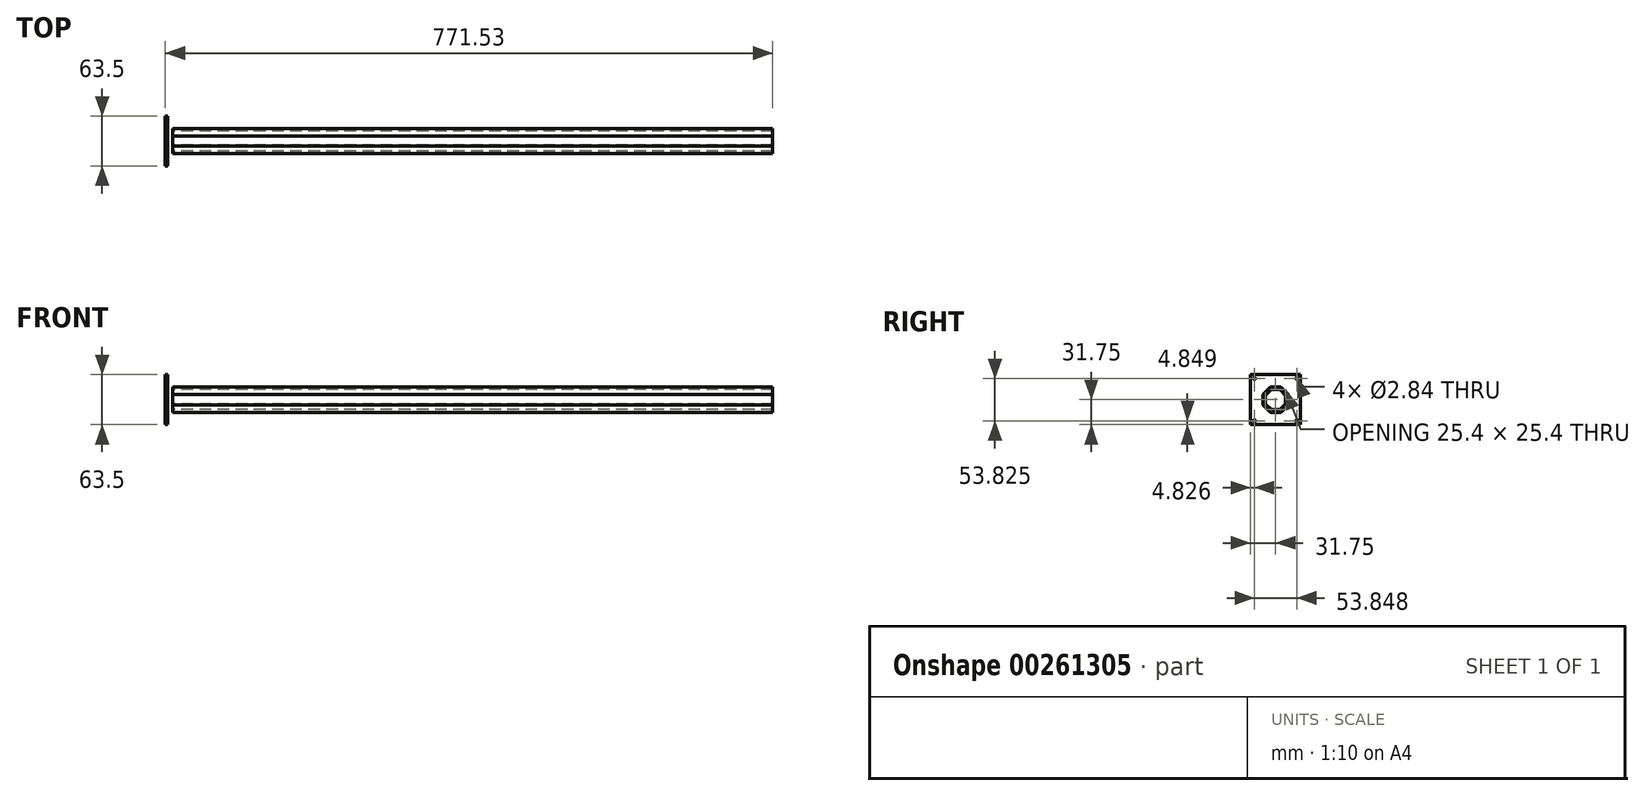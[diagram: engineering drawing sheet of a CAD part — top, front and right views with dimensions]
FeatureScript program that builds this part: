
annotation { "Feature Type Name" : "Feature", "Feature Type Description" : "" }
export const myFeature = defineFeature(function(context is Context, id is Id, definition is map)
    precondition{}
    {
        {
            var Q0;
            Q0=qCreatedBy(makeId("Right.planeOp"),FACE);
            var sketch = newSketch(context, id + "F0", { "sketchPlane" : qUnion([Q0])});
            skCircle(sketch, "E0.cCircle", {"center": v(0, 0) * mm, "radius": 12.7 * mm, "construction": true});
            skLineSegment(sketch, "E0.0", {"start": v(-5.26, 12.7) * mm, "end": v(5.26, 12.7) * mm});
            skLineSegment(sketch, "E0.1", {"start": v(5.26, 12.7) * mm, "end": v(12.7, 5.26) * mm});
            skLineSegment(sketch, "E0.2", {"start": v(12.7, 5.26) * mm, "end": v(12.7, -5.26) * mm});
            skLineSegment(sketch, "E0.3", {"start": v(12.7, -5.26) * mm, "end": v(5.26, -12.7) * mm});
            skLineSegment(sketch, "E0.4", {"start": v(5.26, -12.7) * mm, "end": v(-5.26, -12.7) * mm});
            skLineSegment(sketch, "E0.5", {"start": v(-5.26, -12.7) * mm, "end": v(-12.7, -5.26) * mm});
            skLineSegment(sketch, "E0.6", {"start": v(-12.7, -5.26) * mm, "end": v(-12.7, 5.26) * mm});
            skLineSegment(sketch, "E0.7", {"start": v(-12.7, 5.26) * mm, "end": v(-5.26, 12.7) * mm});
            skPoint(sketch, "E0.0.midPoint", {"position": v(0, 12.7) * mm});
            skCircle(sketch, "E1.cCircle", {"center": v(0, 0) * mm, "radius": 16 * mm, "construction": true});
            skLineSegment(sketch, "E1.0", {"start": v(-6.63, 16) * mm, "end": v(6.63, 16) * mm});
            skLineSegment(sketch, "E1.1", {"start": v(6.63, 16) * mm, "end": v(16, 6.63) * mm});
            skLineSegment(sketch, "E1.2", {"start": v(16, 6.63) * mm, "end": v(16, -6.63) * mm});
            skLineSegment(sketch, "E1.3", {"start": v(16, -6.63) * mm, "end": v(6.63, -16) * mm});
            skLineSegment(sketch, "E1.4", {"start": v(6.63, -16) * mm, "end": v(-6.63, -16) * mm});
            skLineSegment(sketch, "E1.5", {"start": v(-6.63, -16) * mm, "end": v(-16, -6.63) * mm});
            skLineSegment(sketch, "E1.6", {"start": v(-16, -6.63) * mm, "end": v(-16, 6.63) * mm});
            skLineSegment(sketch, "E1.7", {"start": v(-16, 6.63) * mm, "end": v(-6.63, 16) * mm});
            skPoint(sketch, "E1.0.midPoint", {"position": v(0, 16) * mm});
            skSolve(sketch);
        }
        {
            var Q0;
            Q0=makeQuery(id+"F0.imprint","IMPRINT",FACE,{"disambiguationData":[TD([[makeQuery(id+"F0.imprint","IMPRINT",EDGE,{"derivedFrom":sQuery(id+"F0.wireOp",EDGE,"E0.0")}),1.0]])]});
            extrude(context, id + "F1", {"entities" : qUnion([Q0]), "depth" : 762 * mm});
        }
        {
            var Q0;
            Q0=qCreatedBy(makeId("Right.planeOp"),FACE);
            cPlane(context, id + "F2", {"entities" : qUnion([Q0]), "cplaneType" : CPlaneType.OFFSET, "offset" : 6.35 * mm, "oppositeDirection" : true, "width" : 150 * mm, "height" : 150 * mm});
        }
        {
            var Q0;
            Q0=qCreatedBy(id+"F2.planeOp",FACE);
            var sketch = newSketch(context, id + "F3", { "sketchPlane" : qUnion([Q0])});
            skCircle(sketch, "E2", {"center": v(0, 0) * mm, "radius": 19.09 * mm});
            skLineSegment(sketch, "E3", {"start": v(0, 0) * mm, "end": v(0, 22.66) * mm, "construction": true});
            skPoint(sketch, "E4", {"position": v(0, 19.09) * mm});
            skSolve(sketch);
        }
        {
            var Q0;
            Q0=qCreatedBy(makeId("Right.planeOp"),FACE);
            var sketch = newSketch(context, id + "F4", { "sketchPlane" : qUnion([Q0])});
            skCircle(sketch, "E5", {"center": v(0, 0) * mm, "radius": 16 * mm});
            skSolve(sketch);
        }
        {
            var Q0;
            Q0=qCreatedBy(makeId("Front.planeOp"),FACE);
            var sketch = newSketch(context, id + "F5", { "sketchPlane" : qUnion([Q0])});
            skLineSegment(sketch, "E6", {"start": v(0, -16) * mm, "end": v(0, 16) * mm});
            skLineSegment(sketch, "E7.1.0", {"start": v(0, 6.63) * mm, "end": v(0, 16) * mm});
            skLineSegment(sketch, "E7.1.2", {"start": v(0, 16) * mm, "end": v(0, 6.63) * mm});
            skLineSegment(sketch, "E7.1.3", {"start": v(0, 6.63) * mm, "end": v(0, -6.63) * mm});
            skLineSegment(sketch, "E7.1.4", {"start": v(0, -6.63) * mm, "end": v(0, -16) * mm});
            skLineSegment(sketch, "E7.1.6", {"start": v(0, -16) * mm, "end": v(0, -6.63) * mm});
            skLineSegment(sketch, "E7.1.7", {"start": v(0, -6.63) * mm, "end": v(0, 6.63) * mm});
            skLineSegment(sketch, "E8.0", {"start": v(-6.35, 19.09) * mm, "end": v(-6.35, -19.09) * mm});
            skArc(sketch, "E9", {"start": v(-6.35, 19.09) * mm, "mid": v(-3.6, 16.68) * mm, "end": v(0, 16) * mm});
            skSolve(sketch);
        }
        {
            var Q0;
            Q0=sQuery(id+"F4.wireOp",EDGE,"E5");
            var Q1;
            Q1=sQuery(id+"F3.wireOp",EDGE,"E2");
            var Q2;
            Q2=sQuery(id+"F5.wireOp",EDGE,"E9");
            loft(context, id + "F6", {"bodyType" : ToolBodyType.SURFACE, "addGuides" : true, "wireProfilesArray" : [{ "wireProfileEntities" : qUnion([Q0]) }, { "wireProfileEntities" : qUnion([Q1]) }], "guidesArray" : [{ "guideEntities" : qUnion([Q2]), "guideDerivativeType" : LoftGuideDerivativeType.DEFAULT, "guideDerivativeMagnitude" : 1 }]});
        }
        {
            var Q0;
            Q0=qCreatedBy(id+"F2.planeOp",FACE);
            var sketch = newSketch(context, id + "F7", { "sketchPlane" : qUnion([Q0])});
            skPoint(sketch, "E10.middle", {"position": v(0, 0) * mm});
            skArc(sketch, "E11.0", {"start": v(-14.94, -11.87) * mm, "mid": v(-19.09, 0) * mm, "end": v(-14.94, 11.87) * mm});
            skLineSegment(sketch, "E12.trimOffspring", {"start": v(31.75, 31.75) * mm, "end": v(31.75, 32.75) * mm});
            skLineSegment(sketch, "E13.trimOffspring", {"start": v(-31.75, 31.75) * mm, "end": v(-31.75, 32.75) * mm});
            skArc(sketch, "E14.trimOffspring", {"start": v(14.94, 11.87) * mm, "mid": v(19.09, 0) * mm, "end": v(14.94, -11.87) * mm});
            skLineSegment(sketch, "E15.bottom", {"start": v(-31.75, 31.75) * mm, "end": v(31.75, 31.75) * mm});
            skLineSegment(sketch, "E15.top", {"start": v(-31.75, -31.75) * mm, "end": v(31.75, -31.75) * mm});
            skLineSegment(sketch, "E15.left", {"start": v(-31.75, 31.75) * mm, "end": v(-31.75, -31.75) * mm});
            skLineSegment(sketch, "E15.right", {"start": v(31.75, 31.75) * mm, "end": v(31.75, -31.75) * mm});
            skSolve(sketch);
        }
        {
            var Q0;
            Q0 = qSketchRegion(id + "F7", true);
            extrude(context, id + "F8", {"entities" : qUnion([Q0]), "oppositeDirection" : true, "depth" : 3.17 * mm});
        }
        {
            var Q0;
            Q0=makeQuery(id+"F8.opExtrude","CAP_FACE",FACE,{"disambiguationData":[OSD([sQuery(id+"F7.wireOp",EDGE,"E15.bottom"),sQuery(id+"F7.wireOp",EDGE,"E15.top"),sQuery(id+"F7.wireOp",EDGE,"E15.left"),sQuery(id+"F7.wireOp",EDGE,"E15.right")])],"isStart":true});
            var sketch = newSketch(context, id + "F9", { "sketchPlane" : qUnion([Q0])});
            skPoint(sketch, "E16", {"position": v(-26.92, 26.92) * mm});
            skPoint(sketch, "E17", {"position": v(26.92, 26.92) * mm});
            skPoint(sketch, "E18", {"position": v(26.92, -26.9) * mm});
            skPoint(sketch, "E19", {"position": v(-26.92, -26.9) * mm});
            skSolve(sketch);
        }
        {
            var Q0;
            Q0=sQuery(id+"F9.wireOp",VERTEX,"E16");
            var Q1;
            Q1=sQuery(id+"F9.wireOp",VERTEX,"E17");
            var Q2;
            Q2=sQuery(id+"F9.wireOp",VERTEX,"E18");
            var Q3;
            Q3=sQuery(id+"F9.wireOp",VERTEX,"E19");
            var Q4;
            Q4=makeQuery(id+"F8.opExtrude","SWEPT_BODY",BODY,{"disambiguationData":[OSD([sQuery(id+"F7.wireOp",EDGE,"E15.bottom"),sQuery(id+"F7.wireOp",EDGE,"E15.top"),sQuery(id+"F7.wireOp",EDGE,"E15.left"),sQuery(id+"F7.wireOp",EDGE,"E15.right")])]});
            hole(context, id + "F10", {"style" : HoleStyle.SIMPLE, "endStyle" : HoleEndStyle.THROUGH, "holeDiameter" : 2.84 * mm, "tappedDepth" : 12 * mm, "tapClearance" : 3, "locations" : qUnion([Q0, Q1, Q2, Q3]), "scope" : qUnion([Q4])});
        }
    });
